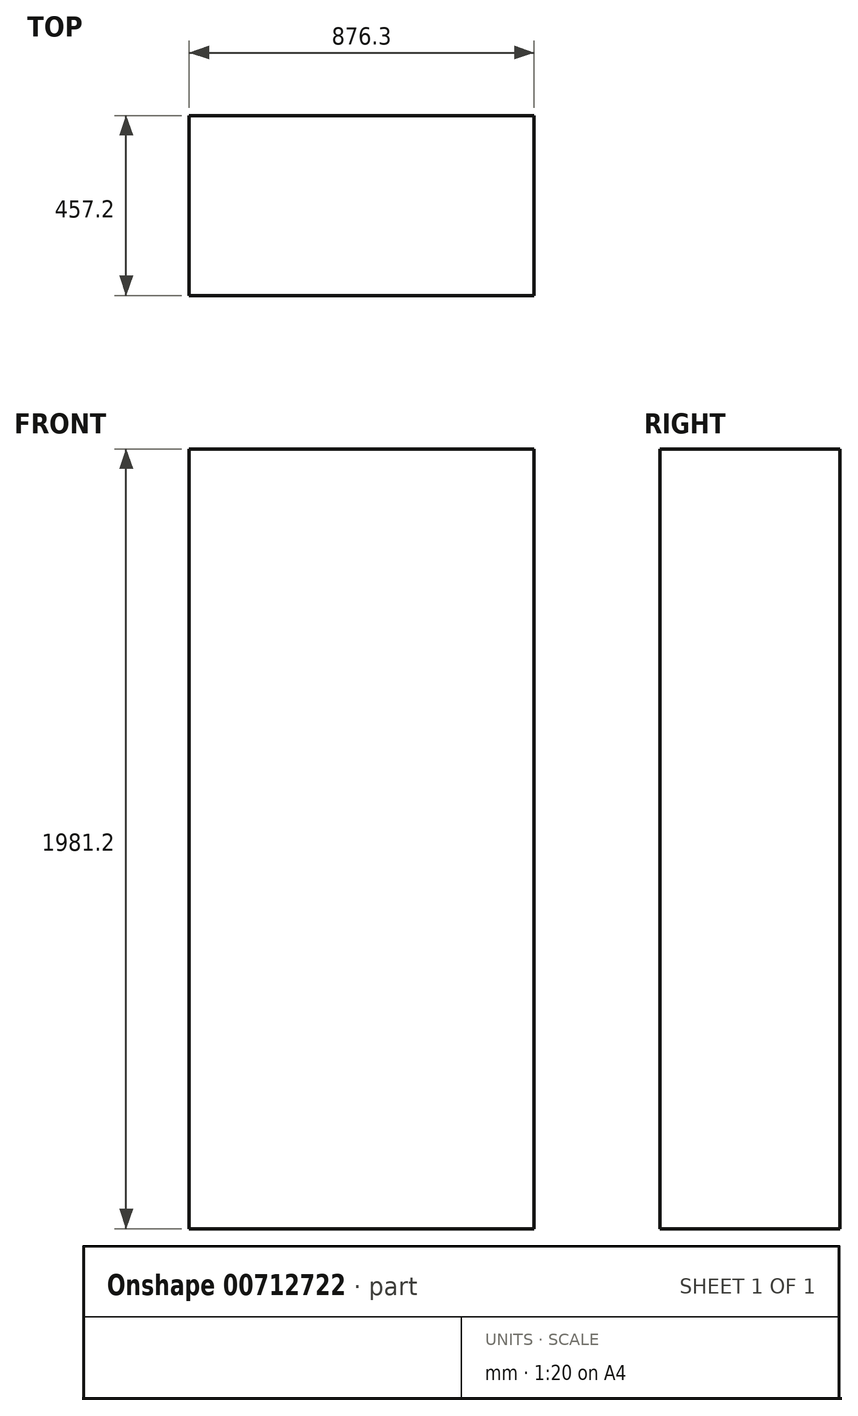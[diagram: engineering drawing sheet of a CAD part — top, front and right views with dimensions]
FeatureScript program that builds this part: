
annotation { "Feature Type Name" : "Feature", "Feature Type Description" : "" }
export const myFeature = defineFeature(function(context is Context, id is Id, definition is map)
    precondition{}
    {
        {
            var Q0;
            Q0=qCreatedBy(makeId("Top.planeOp"),FACE);
            var sketch = newSketch(context, id + "F0", { "sketchPlane" : qUnion([Q0])});
            skLineSegment(sketch, "E0.bottom", {"start": v(0, 0) * mm, "end": v(876.3, 0) * mm});
            skLineSegment(sketch, "E0.top", {"start": v(0, 457.2) * mm, "end": v(876.3, 457.2) * mm});
            skLineSegment(sketch, "E0.left", {"start": v(0, 0) * mm, "end": v(0, 457.2) * mm});
            skLineSegment(sketch, "E0.right", {"start": v(876.3, 0) * mm, "end": v(876.3, 457.2) * mm});
            skSolve(sketch);
        }
        {
            var Q0;
            Q0=qSketchRegion(id+"F0",true);
            extrude(context, id + "F1", {"entities" : qUnion([Q0]), "depth" : 1981.2 * mm, "offsetDistance" : 25.4 * mm});
        }
    });
